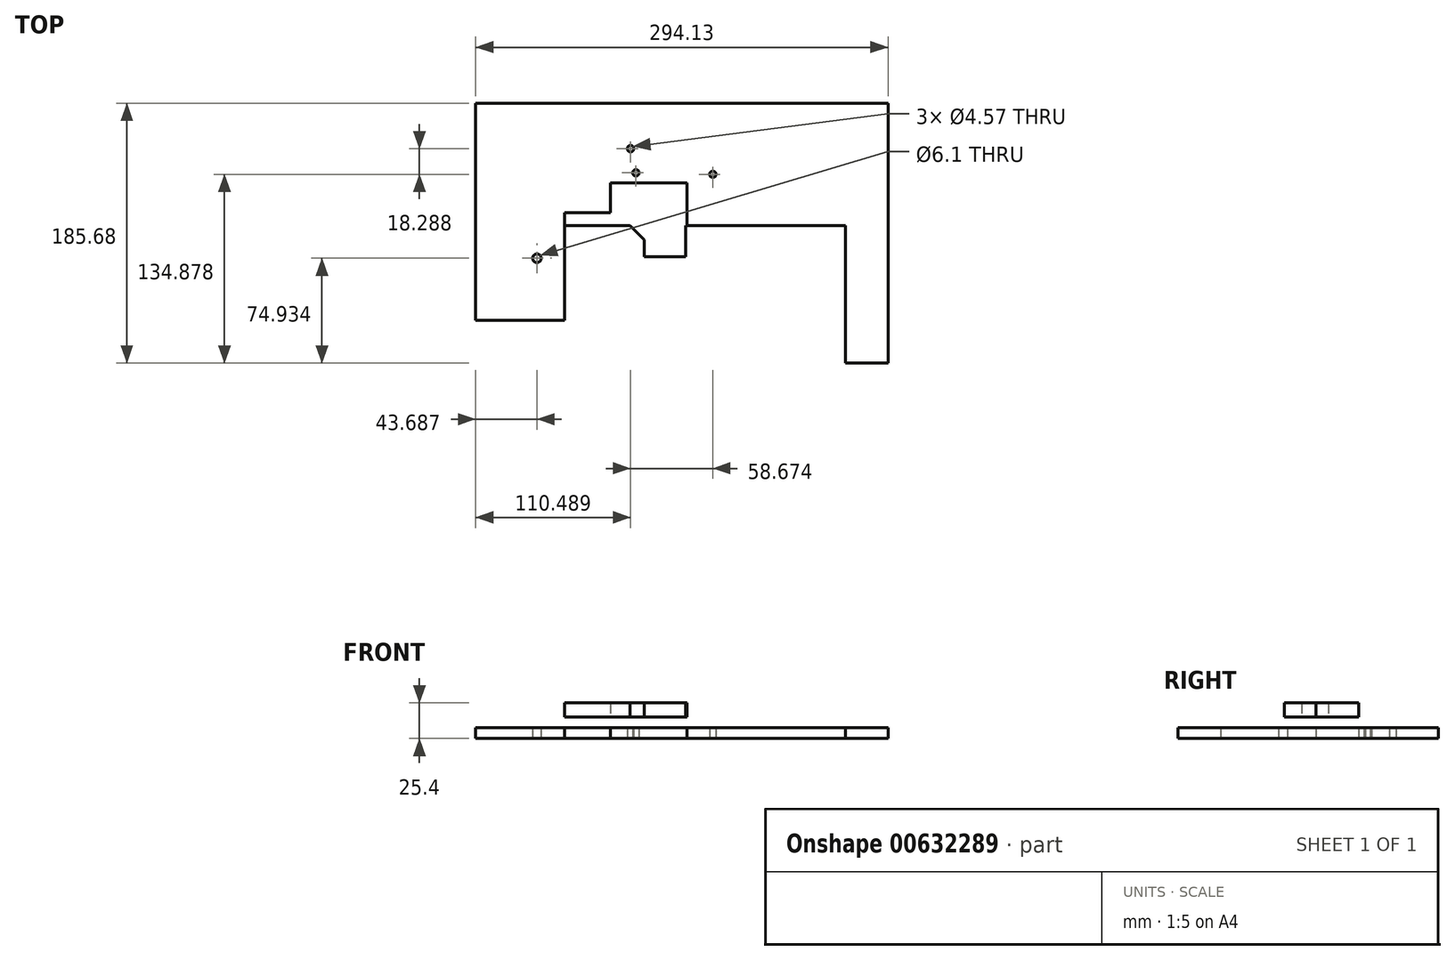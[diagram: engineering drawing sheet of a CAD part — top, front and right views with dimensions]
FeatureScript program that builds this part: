
annotation { "Feature Type Name" : "Feature", "Feature Type Description" : "" }
export const myFeature = defineFeature(function(context is Context, id is Id, definition is map)
    precondition{}
    {
        {
            var Q0;
            Q0=qCreatedBy(makeId("Top.planeOp"),FACE);
            var sketch = newSketch(context, id + "F0", { "sketchPlane" : qUnion([Q0])});
            skLineSegment(sketch, "E0", {"start": v(-14.86, 0) * mm, "end": v(14.86, 0) * mm});
            skLineSegment(sketch, "E1", {"start": v(-14.86, 0) * mm, "end": v(-14.86, 12.2) * mm});
            skLineSegment(sketch, "E2", {"start": v(-14.86, 12.2) * mm, "end": v(-24.77, 22.35) * mm});
            skLineSegment(sketch, "E3", {"start": v(-24.77, 22.35) * mm, "end": v(14.86, 22.35) * mm});
            skLineSegment(sketch, "E4", {"start": v(14.86, 22.35) * mm, "end": v(14.86, 0) * mm});
            skLineSegment(sketch, "E5", {"start": v(14.86, 22.35) * mm, "end": v(15.88, 22.35) * mm});
            skLineSegment(sketch, "E6", {"start": v(15.88, 22.35) * mm, "end": v(15.87, 52.83) * mm});
            skLineSegment(sketch, "E7", {"start": v(15.87, 52.83) * mm, "end": v(-38.99, 52.83) * mm});
            skLineSegment(sketch, "E8", {"start": v(-38.99, 52.83) * mm, "end": v(-38.99, 22.35) * mm});
            skLineSegment(sketch, "E9", {"start": v(-38.99, 22.35) * mm, "end": v(-24.77, 22.35) * mm});
            skLineSegment(sketch, "E10", {"start": v(-38.99, 22.35) * mm, "end": v(-71.5, 22.35) * mm});
            skLineSegment(sketch, "E11", {"start": v(-71.5, 22.35) * mm, "end": v(-71.5, -45.47) * mm});
            skLineSegment(sketch, "E12", {"start": v(15.88, 22.35) * mm, "end": v(128.65, 22.35) * mm});
            skLineSegment(sketch, "E13", {"start": v(128.65, 22.35) * mm, "end": v(128.65, -45.47) * mm});
            skLineSegment(sketch, "E14", {"start": v(128.65, -45.47) * mm, "end": v(-71.5, -45.47) * mm});
            skLineSegment(sketch, "E15", {"start": v(-71.5, -45.47) * mm, "end": v(-135, -45.47) * mm});
            skLineSegment(sketch, "E16", {"start": v(-135, -45.47) * mm, "end": v(-135, 109.73) * mm});
            skLineSegment(sketch, "E17", {"start": v(-135, 109.73) * mm, "end": v(159.13, 109.73) * mm});
            skLineSegment(sketch, "E18", {"start": v(159.13, 109.73) * mm, "end": v(159.13, -75.95) * mm});
            skLineSegment(sketch, "E19", {"start": v(159.13, -75.95) * mm, "end": v(128.65, -75.95) * mm});
            skLineSegment(sketch, "E20", {"start": v(128.65, -75.95) * mm, "end": v(128.65, -45.47) * mm});
            skCircle(sketch, "E21", {"center": v(-20.7, 59.94) * mm, "radius": 2.29 * mm});
            skCircle(sketch, "E22", {"center": v(-24.51, 77.22) * mm, "radius": 2.29 * mm});
            skCircle(sketch, "E23", {"center": v(34.16, 58.93) * mm, "radius": 2.29 * mm});
            skCircle(sketch, "E24", {"center": v(-91.31, -1.02) * mm, "radius": 3.05 * mm});
            skSolve(sketch);
        }
        {
            var Q0;
            Q0=qCreatedBy(makeId("Top.planeOp"),FACE);
            cPlane(context, id + "F1", {"entities" : qUnion([Q0]), "cplaneType" : CPlaneType.OFFSET, "offset" : 15.24 * mm, "width" : 152.4 * mm, "height" : 152.4 * mm});
        }
        {
            var Q0;
            Q0=makeQuery(id+"F0.imprint","IMPRINT",FACE,{"disambiguationData":[TD([[makeQuery(id+"F0.imprint","IMPRINT",EDGE,{"derivedFrom":sQuery(id+"F0.wireOp",EDGE,"E6")}),-1.0]])]});
            extrude(context, id + "F2", {"entities" : qUnion([Q0]), "depth" : 7.62 * mm, "offsetDistance" : 25.4 * mm});
        }
        {
            var Q0;
            Q0=qCreatedBy(id+"F1.planeOp",FACE);
            var sketch = newSketch(context, id + "F3", { "sketchPlane" : qUnion([Q0])});
            skLineSegment(sketch, "E25.bottom", {"start": v(-38.99, 22.35) * mm, "end": v(-71.5, 22.35) * mm});
            skLineSegment(sketch, "E25.top", {"start": v(-38.99, 31.5) * mm, "end": v(-71.5, 31.5) * mm});
            skLineSegment(sketch, "E25.left", {"start": v(-38.99, 22.35) * mm, "end": v(-38.99, 31.5) * mm});
            skLineSegment(sketch, "E25.right", {"start": v(-71.5, 22.35) * mm, "end": v(-71.5, 31.5) * mm});
            skLineSegment(sketch, "E26.bottom", {"start": v(-38.99, 52.83) * mm, "end": v(15.88, 52.83) * mm});
            skLineSegment(sketch, "E26.top", {"start": v(-38.99, 22.35) * mm, "end": v(15.88, 22.35) * mm});
            skLineSegment(sketch, "E26.left", {"start": v(-38.99, 52.83) * mm, "end": v(-38.99, 22.35) * mm});
            skLineSegment(sketch, "E26.right", {"start": v(15.88, 52.83) * mm, "end": v(15.88, 22.35) * mm});
            skLineSegment(sketch, "E27", {"start": v(14.86, 0) * mm, "end": v(-14.86, 0) * mm});
            skLineSegment(sketch, "E28", {"start": v(-14.86, 0) * mm, "end": v(-14.86, 12.2) * mm});
            skLineSegment(sketch, "E29", {"start": v(-14.86, 12.2) * mm, "end": v(-24.77, 22.35) * mm});
            skLineSegment(sketch, "E30", {"start": v(-24.77, 22.35) * mm, "end": v(14.86, 22.35) * mm});
            skLineSegment(sketch, "E31", {"start": v(14.86, 22.35) * mm, "end": v(14.86, 0) * mm});
            skSolve(sketch);
        }
        {
            var Q0;
            {var subQ1=sQuery(id+"F3.wireOp",EDGE,"E25.left");var subQ2=sQuery(id+"F3.wireOp",EDGE,"E25.bottom");var subQ8=makeQuery(id+"F3.imprint","IMPRINT",EDGE,{"derivedFrom":subQ1});Q0=qUnion([makeQuery(id+"F3.imprint","IMPRINT",FACE,{"disambiguationData":[TD([[makeQuery(id+"F3.imprint","IMPRINT",EDGE,{"derivedFrom":subQ2}),-1.0]])]}),makeQuery(id+"F3.imprint","IMPRINT",FACE,{"disambiguationData":[TD([[makeQuery(id+"F3.imprint","IMPRINT",EDGE,{"derivedFrom":sQuery(id+"F3.wireOp",EDGE,"E27")}),-1.0]])]}),makeQuery(id+"F3.imprint","IMPRINT",FACE,{"disambiguationData":[TD([[subQ8,-1.0]])]})]);}
            extrude(context, id + "F4", {"entities" : qUnion([Q0]), "depth" : 10.16 * mm, "offsetDistance" : 25.4 * mm});
        }
    });
